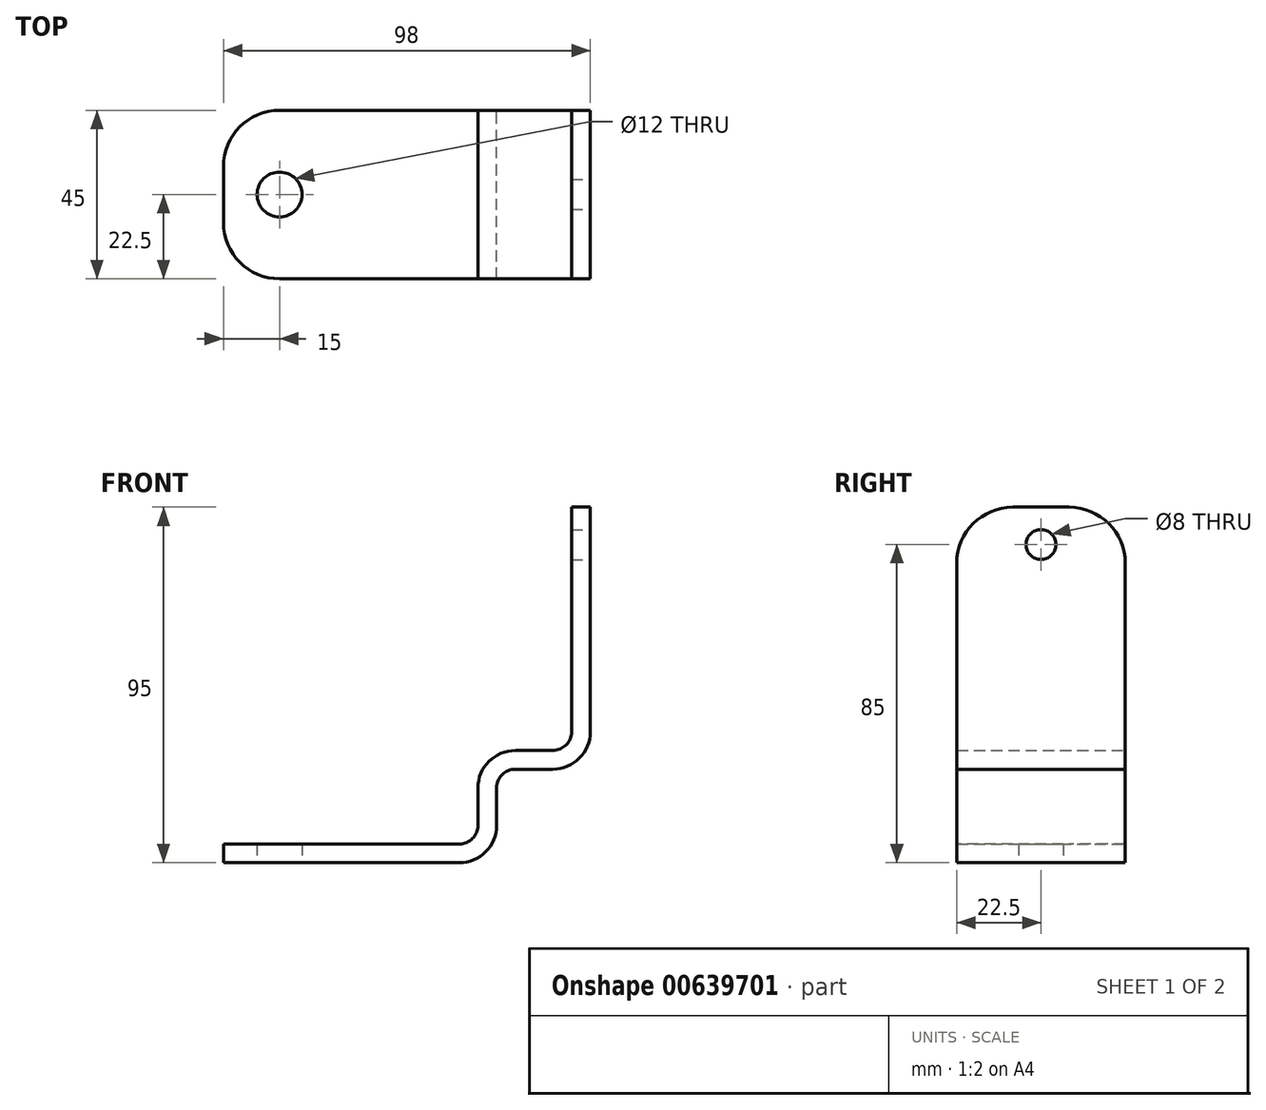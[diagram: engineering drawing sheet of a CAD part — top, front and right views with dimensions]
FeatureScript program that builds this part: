
annotation { "Feature Type Name" : "Feature", "Feature Type Description" : "" }
export const myFeature = defineFeature(function(context is Context, id is Id, definition is map)
    precondition{}
    {
        {
            var Q0;
            Q0=qCreatedBy(makeId("Front.planeOp"),FACE);
            var sketch = newSketch(context, id + "F0", { "sketchPlane" : qUnion([Q0])});
            skLineSegment(sketch, "E0", {"start": v(0, 95) * mm, "end": v(0, 35) * mm});
            skLineSegment(sketch, "E1", {"start": v(-10, 25) * mm, "end": v(-20, 25) * mm});
            skLineSegment(sketch, "E2", {"start": v(-25, 20) * mm, "end": v(-25, 10) * mm});
            skLineSegment(sketch, "E3", {"start": v(-35, 0) * mm, "end": v(-98, 0) * mm});
            skLineSegment(sketch, "E4", {"start": v(-98, 0) * mm, "end": v(-98, 5) * mm});
            skLineSegment(sketch, "E5", {"start": v(-98, 5) * mm, "end": v(-35, 5) * mm});
            skLineSegment(sketch, "E6", {"start": v(-30, 10) * mm, "end": v(-30, 20) * mm});
            skLineSegment(sketch, "E7", {"start": v(-20, 30) * mm, "end": v(-10, 30) * mm});
            skLineSegment(sketch, "E8", {"start": v(-5, 35) * mm, "end": v(-5, 95) * mm});
            skLineSegment(sketch, "E9", {"start": v(-5, 95) * mm, "end": v(0, 95) * mm});
            skPoint(sketch, "E10.visualSharp", {"position": v(-5, 30) * mm});
            skArc(sketch, "E10.filletArc", {"start": v(-10, 30) * mm, "mid": v(-6.46, 31.46) * mm, "end": v(-5, 35) * mm});
            skPoint(sketch, "E11.visualSharp", {"position": v(-30, 5) * mm});
            skArc(sketch, "E11.filletArc", {"start": v(-35, 5) * mm, "mid": v(-31.46, 6.46) * mm, "end": v(-30, 10) * mm});
            skPoint(sketch, "E12.visualSharp", {"position": v(-25, 25) * mm});
            skArc(sketch, "E12.filletArc", {"start": v(-20, 25) * mm, "mid": v(-23.54, 23.54) * mm, "end": v(-25, 20) * mm});
            skPoint(sketch, "E13.visualSharp", {"position": v(0, 25) * mm});
            skArc(sketch, "E13.filletArc", {"start": v(-10, 25) * mm, "mid": v(-2.93, 27.93) * mm, "end": v(0, 35) * mm});
            skPoint(sketch, "E14.visualSharp", {"position": v(-30, 30) * mm});
            skArc(sketch, "E14.filletArc", {"start": v(-20, 30) * mm, "mid": v(-27.07, 27.07) * mm, "end": v(-30, 20) * mm});
            skPoint(sketch, "E15.visualSharp", {"position": v(-25, 0) * mm});
            skArc(sketch, "E15.filletArc", {"start": v(-35, 0) * mm, "mid": v(-27.93, 2.93) * mm, "end": v(-25, 10) * mm});
            skSolve(sketch);
        }
        {
            var Q0;
            Q0=makeQuery(id+"F0.imprint","IMPRINT",FACE,{"disambiguationData":[TD([[makeQuery(id+"F0.imprint","IMPRINT",EDGE,{"derivedFrom":sQuery(id+"F0.wireOp",EDGE,"E0")}),-1.0]])]});
            extrude(context, id + "F1", {"entities" : qUnion([Q0]), "endBound" : BoundingType.SYMMETRIC, "depth" : 45 * mm, "offsetDistance" : 25 * mm});
        }
        {
            var Q0;
            Q0=makeQuery(id+"F1.opExtrude","CAP_EDGE",EDGE,{"disambiguationData":[OSD([sQuery(id+"F0.wireOp",EDGE,"E4")])],"isStart":false});
            var Q1;
            Q1=makeQuery(id+"F1.opExtrude","CAP_EDGE",EDGE,{"disambiguationData":[OSD([sQuery(id+"F0.wireOp",EDGE,"E9")])],"isStart":false});
            var Q2;
            Q2=makeQuery(id+"F1.opExtrude","CAP_EDGE",EDGE,{"disambiguationData":[OSD([sQuery(id+"F0.wireOp",EDGE,"E9")])],"isStart":true});
            var Q3;
            Q3=makeQuery(id+"F1.opExtrude","CAP_EDGE",EDGE,{"disambiguationData":[OSD([sQuery(id+"F0.wireOp",EDGE,"E4")])],"isStart":true});
            fillet(context, id + "F2", {"entities" : qUnion([Q0, Q1, Q2, Q3]), "radius" : 15 * mm, "tangentPropagation" : true, "allowEdgeOverflow" : false});
        }
        {
            var Q0;
            Q0=makeQuery(id+"F1.opExtrude","SWEPT_FACE",FACE,{"disambiguationData":[OSD([sQuery(id+"F0.wireOp",EDGE,"E0")])]});
            var sketch = newSketch(context, id + "F3", { "sketchPlane" : qUnion([Q0])});
            skCircle(sketch, "E16", {"center": v(0, 85) * mm, "radius": 4 * mm});
            skSolve(sketch);
        }
        {
            var Q0;
            Q0=makeQuery(id+"F3.imprint","IMPRINT",FACE,{"disambiguationData":[TD([[makeQuery(id+"F3.imprint","IMPRINT",EDGE,{"derivedFrom":sQuery(id+"F3.wireOp",EDGE,"E16")}),1.0]])]});
            extrude(context, id + "F4", {"entities" : qUnion([Q0]), "operationType" : NewBodyOperationType.REMOVE, "endBound" : BoundingType.THROUGH_ALL, "oppositeDirection" : true, "depth" : 25 * mm, "offsetDistance" : 25 * mm});
        }
        {
            var Q0;
            Q0=qCreatedBy(makeId("Top.planeOp"),FACE);
            var sketch = newSketch(context, id + "F5", { "sketchPlane" : qUnion([Q0])});
            skCircle(sketch, "E17", {"center": v(-83, 0) * mm, "radius": 6 * mm});
            skSolve(sketch);
        }
        {
            var Q0;
            Q0=makeQuery(id+"F5.imprint","IMPRINT",FACE,{"disambiguationData":[TD([[makeQuery(id+"F5.imprint","IMPRINT",EDGE,{"derivedFrom":sQuery(id+"F5.wireOp",EDGE,"E17")}),1.0]])]});
            extrude(context, id + "F6", {"entities" : qUnion([Q0]), "operationType" : NewBodyOperationType.REMOVE, "depth" : 25 * mm, "offsetDistance" : 25 * mm});
        }
    });
